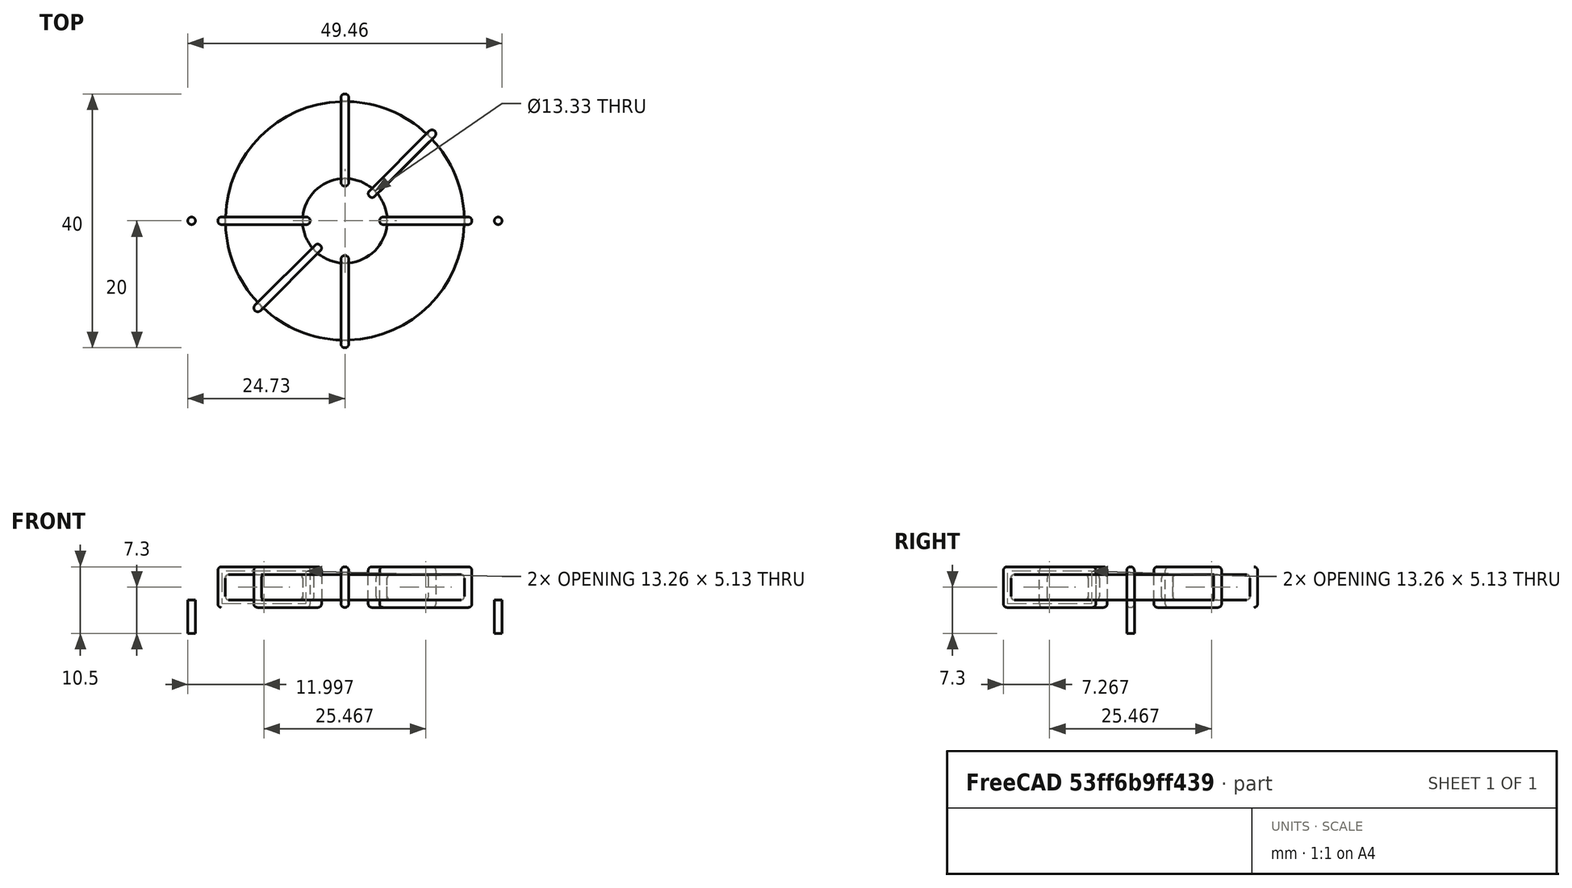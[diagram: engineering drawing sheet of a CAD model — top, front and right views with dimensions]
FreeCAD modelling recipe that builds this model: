
FCSTD DOCUMENT  (FreeCAD 0.16R6703 (Git))
Label: L_Toroid_Horizontal_D40.0mm_P48.26mm
License: All rights reserved
LicenseURL: http://en.wikipedia.org/wiki/All_rights_reserved
objects: Sketcher::SketchObject×6, PartDesign::Pad×6, PartDesign::Fillet×5, Spreadsheet::Sheet×1
note: 23 computed .brp shape members not serialized (recipe doc carries the construction recipe); baked Part::Feature solids carry a one-line shape summary decoded from their .brp

FEATURE [Spreadsheet::Sheet] Spreadsheet  label="dimensions"
  cells = A1=Wx; B1(Wx)=40; C1(WW)=13.33333333333333; D1=40; A2=Wy; B2(Wy)=40; D2=40; A3=RM; B3(RMx)=48.26; C3(RMy)=0; A4=d_wire; B4(d_wire)=1.2; A5=H; B5(H)=4; A6=offsetx; B6(offsetx)=-4.129999999999999
FEATURE [Sketcher::SketchObject] Sketch
  Placement = pos=(0,0,1.7) rot=(0,0,1;0rad)
  expr: Placement.Base.z = 0.5 + Spreadsheet.d_wire
  expr: Constraints[0] = Spreadsheet.Wx / 2 - Spreadsheet.d_wire
  expr: Constraints[4] = Spreadsheet.WW / 2
  expr: Constraints[2] = Spreadsheet.RMy / 2
  expr: Constraints[1] = Spreadsheet.RMx / 2
  sketch-geometry (2):
    g0: Circle CenterX=24.13 CenterY=0 CenterZ=0 NormalX=0 NormalY=0 NormalZ=1 Radius=18.8
    g1: Circle CenterX=24.13 CenterY=0 CenterZ=0 NormalX=0 NormalY=0 NormalZ=1 Radius=6.66667
  constraints (5):
    c: Radius(g0) = 18.8
    c: DistanceX(g-1,g0) = 24.13
    c: DistanceY(g-1,g0) = 0
    c: Coincident(g1,g0)
    c: Radius(g1) = 6.66667
FEATURE [PartDesign::Pad] Pad
  Length = 4
  Length2 = 100
  Placement = pos=(0,0,1.7) rot=(0,0,1;0rad)
  Sketch = -> Sketch
  Type = 0
  expr: Length = Spreadsheet.H
FEATURE [Sketcher::SketchObject] Sketch001
  Placement = pos=(0,0,1.1) rot=(0,0,1;0rad)
  expr: Placement.Base.z = 0.5 + Spreadsheet.d_wire * 0.5
  expr: Constraints[4] = Spreadsheet.RMx
  expr: Constraints[2] = Spreadsheet.RMy
  expr: Constraints[1] = Spreadsheet.d_wire / 2
  sketch-geometry (2):
    g0: Circle CenterX=0 CenterY=0 CenterZ=0 NormalX=0 NormalY=0 NormalZ=1 Radius=0.6
    g1: Circle CenterX=48.26 CenterY=0 CenterZ=0 NormalX=0 NormalY=0 NormalZ=1 Radius=0.6
  constraints (5):
    c: Equal(g0,g1)
    c: Radius(g0) = 0.6
    c: DistanceY(g-1,g1) = 0
    c: Coincident(g0,g-1)
    c: DistanceX(g-1,g1) = 48.26
FEATURE [PartDesign::Pad] Pad001
  Length = 0.6
  Length2 = 4.7
  Placement = pos=(0,0,1.1) rot=(0,0,1;0rad)
  Reversed = true
  Sketch = -> Sketch001
  Type = 4
  expr: Length2 = 3.5 + Spreadsheet.d_wire
  expr: Length = Spreadsheet.d_wire / 2
FEATURE [PartDesign::Fillet] Fillet
  Base = -> Pad [Edge6,Edge3,Edge2]
  Placement = pos=(0,0,1.7) rot=(0,0,1;0rad)
  Radius = 0.5
FEATURE [Sketcher::SketchObject] Sketch003
  Placement = pos=(24.13,0,0) rot=(1,0,0;1.5708rad)
  expr: Placement.Base.x = Spreadsheet.RMx / 2
  expr: Constraints[49] = Spreadsheet.Wx - Spreadsheet.d_wire * 2
  expr: Constraints[44] = Spreadsheet.d_wire
  expr: Constraints[23] = Spreadsheet.H
  expr: Constraints[22] = Spreadsheet.Wx / 2 - Spreadsheet.d_wire
  expr: Placement.Base.y = Spreadsheet.RMy / 2
  expr: Constraints[21] = (Spreadsheet.Wx - Spreadsheet.WW) / 2 - Spreadsheet.d_wire
  expr: Constraints[19] = Spreadsheet.d_wire
  expr: Constraints[17] = Spreadsheet.d_wire
  expr: Constraints[18] = Spreadsheet.d_wire
  expr: Constraints[16] = Spreadsheet.d_wire
  sketch-geometry (16):
    g0: LineSegment StartX=-5.46667 StartY=0.5 StartZ=0 EndX=-20 EndY=0.5 EndZ=0
    g1: LineSegment StartX=-20 StartY=0.5 StartZ=0 EndX=-20 EndY=6.9 EndZ=0
    g2: LineSegment StartX=-20 StartY=6.9 StartZ=0 EndX=-5.46667 EndY=6.9 EndZ=0
    g3: LineSegment StartX=-5.46667 StartY=6.9 StartZ=0 EndX=-5.46667 EndY=0.5 EndZ=0
    g4: LineSegment StartX=-18.8 StartY=5.7 StartZ=0 EndX=-6.66667 EndY=5.7 EndZ=0
    g5: LineSegment StartX=-6.66667 StartY=5.7 StartZ=0 EndX=-6.66667 EndY=1.7 EndZ=0
    g6: LineSegment StartX=-6.66667 StartY=1.7 StartZ=0 EndX=-18.8 EndY=1.7 EndZ=0
    g7: LineSegment StartX=-18.8 StartY=1.7 StartZ=0 EndX=-18.8 EndY=5.7 EndZ=0
    g8: LineSegment StartX=5.46667 StartY=6.9 StartZ=0 EndX=20 EndY=6.9 EndZ=0
    g9: LineSegment StartX=20 StartY=6.9 StartZ=0 EndX=20 EndY=0.5 EndZ=0
    g10: LineSegment StartX=20 StartY=0.5 StartZ=0 EndX=5.46667 EndY=0.5 EndZ=0
    g11: LineSegment StartX=5.46667 StartY=0.5 StartZ=0 EndX=5.46667 EndY=6.9 EndZ=0
    g12: LineSegment StartX=6.66667 StartY=5.7 StartZ=0 EndX=18.8 EndY=5.7 EndZ=0
    g13: LineSegment StartX=18.8 StartY=5.7 StartZ=0 EndX=18.8 EndY=1.7 EndZ=0
    g14: LineSegment StartX=18.8 StartY=1.7 StartZ=0 EndX=6.66667 EndY=1.7 EndZ=0
    g15: LineSegment StartX=6.66667 StartY=1.7 StartZ=0 EndX=6.66667 EndY=5.7 EndZ=0
  constraints (50):
    c: Horizontal(g0)
    c: Coincident(g1,g0)
    c: Vertical(g1)
    c: Coincident(g2,g1)
    c: Horizontal(g2)
    c: Coincident(g3,g2)
    c: Coincident(g3,g0)
    c: Vertical(g3)
    c: Coincident(g4,g5)
    c: Coincident(g5,g6)
    c: Coincident(g6,g7)
    c: Coincident(g7,g4)
    c: Horizontal(g4)
    c: Horizontal(g6)
    c: Vertical(g5)
    c: Vertical(g7)
    c: DistanceX(g1,g4) = 1.2
    c: DistanceY(g4,g1) = 1.2
    c: DistanceX(g5,g0) = 1.2
    c: DistanceY(g0,g5) = 1.2
    c: DistanceY(g-1,g0) = 0.5
    c: DistanceX(g6,g6) = 12.1333
    c: DistanceX(g6,g-1) = 18.8
    c: DistanceY(g7,g7) = 4
    c: Coincident(g8,g9)
    c: Coincident(g9,g10)
    c: Coincident(g10,g11)
    c: Coincident(g11,g8)
    c: Horizontal(g8)
    c: Horizontal(g10)
    c: Vertical(g9)
    c: Vertical(g11)
    c: Coincident(g12,g13)
    c: Coincident(g13,g14)
    c: Coincident(g14,g15)
    c: Coincident(g15,g12)
    c: Horizontal(g12)
    c: Horizontal(g14)
    c: Vertical(g13)
    c: Vertical(g15)
    c: DistanceY(g8,g2) = 0
    c: DistanceY(g10,g0) = 0
    c: DistanceY(g14,g5) = 0
    c: DistanceY(g12,g4) = 0
    c: DistanceX(g8,g12) = 1.2
    c: Equal(g8,g2)
    c: Equal(g12,g4)
    c: Equal(g9,g1)
    c: Equal(g13,g7)
    c: DistanceX(g4,g12) = 37.6
FEATURE [PartDesign::Pad] Pad002
  Length = 1.2
  Length2 = 100
  Midplane = true
  Placement = pos=(24.13,0,0) rot=(1,0,0;1.5708rad)
  Sketch = -> Sketch003
  Type = 0
  expr: Length = Spreadsheet.d_wire
FEATURE [PartDesign::Fillet] Fillet001
  Base = -> Pad002 [Edge38,Edge41,Edge42,Edge43,Edge29,Edge32,Edge33,Edge34,Edge25,Edge35,Edge36,Edge13,Edge14,Edge15,Edge16,Edge17,Edge18,Edge19,Edge1,Edge2,Edge3,Edge4,Edge5,Edge6,Edge7,Edge37,Edge39,Edge40,Edge20,Edge23,Edge24,Edge21,Edge22,Edge8,Edge9,Edge10,Edge11,Edge12,Edge26,Edge27,+8 more]
  Placement = pos=(24.13,0,0) rot=(1,0,0;1.5708rad)
  Radius = 0.564
  expr: Radius = Spreadsheet.d_wire * 0.47
FEATURE [Sketcher::SketchObject] Sketch004
  Placement = pos=(24.13,0,0) rot=(0.862856,0.357407,0.357407;1.71777rad)
  expr: Placement.Base.x = Spreadsheet.RMx / 2
  expr: Constraints[49] = Spreadsheet.Wx - 2 * Spreadsheet.d_wire
  expr: Constraints[44] = Spreadsheet.d_wire
  expr: Constraints[23] = Spreadsheet.H
  expr: Constraints[22] = Spreadsheet.Wx / 2 - Spreadsheet.d_wire
  expr: Placement.Base.y = Spreadsheet.RMy / 2
  expr: Constraints[21] = (Spreadsheet.Wx - Spreadsheet.WW) / 2 - Spreadsheet.d_wire
  expr: Constraints[19] = Spreadsheet.d_wire
  expr: Constraints[17] = Spreadsheet.d_wire
  expr: Constraints[18] = Spreadsheet.d_wire
  expr: Constraints[16] = Spreadsheet.d_wire
  sketch-geometry (16):
    g0: LineSegment StartX=-5.46667 StartY=0.5 StartZ=0 EndX=-20 EndY=0.5 EndZ=0
    g1: LineSegment StartX=-20 StartY=0.5 StartZ=0 EndX=-20 EndY=6.9 EndZ=0
    g2: LineSegment StartX=-20 StartY=6.9 StartZ=0 EndX=-5.46667 EndY=6.9 EndZ=0
    g3: LineSegment StartX=-5.46667 StartY=6.9 StartZ=0 EndX=-5.46667 EndY=0.5 EndZ=0
    g4: LineSegment StartX=-18.8 StartY=5.7 StartZ=0 EndX=-6.66667 EndY=5.7 EndZ=0
    g5: LineSegment StartX=-6.66667 StartY=5.7 StartZ=0 EndX=-6.66667 EndY=1.7 EndZ=0
    g6: LineSegment StartX=-6.66667 StartY=1.7 StartZ=0 EndX=-18.8 EndY=1.7 EndZ=0
    g7: LineSegment StartX=-18.8 StartY=1.7 StartZ=0 EndX=-18.8 EndY=5.7 EndZ=0
    g8: LineSegment StartX=5.46667 StartY=6.9 StartZ=0 EndX=20 EndY=6.9 EndZ=0
    g9: LineSegment StartX=20 StartY=6.9 StartZ=0 EndX=20 EndY=0.5 EndZ=0
    g10: LineSegment StartX=20 StartY=0.5 StartZ=0 EndX=5.46667 EndY=0.5 EndZ=0
    g11: LineSegment StartX=5.46667 StartY=0.5 StartZ=0 EndX=5.46667 EndY=6.9 EndZ=0
    g12: LineSegment StartX=6.66667 StartY=5.7 StartZ=0 EndX=18.8 EndY=5.7 EndZ=0
    g13: LineSegment StartX=18.8 StartY=5.7 StartZ=0 EndX=18.8 EndY=1.7 EndZ=0
    g14: LineSegment StartX=18.8 StartY=1.7 StartZ=0 EndX=6.66667 EndY=1.7 EndZ=0
    g15: LineSegment StartX=6.66667 StartY=1.7 StartZ=0 EndX=6.66667 EndY=5.7 EndZ=0
  constraints (50):
    c: Horizontal(g0)
    c: Coincident(g1,g0)
    c: Vertical(g1)
    c: Coincident(g2,g1)
    c: Horizontal(g2)
    c: Coincident(g3,g2)
    c: Coincident(g3,g0)
    c: Vertical(g3)
    c: Coincident(g4,g5)
    c: Coincident(g5,g6)
    c: Coincident(g6,g7)
    c: Coincident(g7,g4)
    c: Horizontal(g4)
    c: Horizontal(g6)
    c: Vertical(g5)
    c: Vertical(g7)
    c: DistanceX(g1,g4) = 1.2
    c: DistanceY(g4,g1) = 1.2
    c: DistanceX(g5,g0) = 1.2
    c: DistanceY(g0,g5) = 1.2
    c: DistanceY(g-1,g0) = 0.5
    c: DistanceX(g6,g6) = 12.1333
    c: DistanceX(g6,g-1) = 18.8
    c: DistanceY(g7,g7) = 4
    c: Coincident(g8,g9)
    c: Coincident(g9,g10)
    c: Coincident(g10,g11)
    c: Coincident(g11,g8)
    c: Horizontal(g8)
    c: Horizontal(g10)
    c: Vertical(g9)
    c: Vertical(g11)
    c: Coincident(g12,g13)
    c: Coincident(g13,g14)
    c: Coincident(g14,g15)
    c: Coincident(g15,g12)
    c: Horizontal(g12)
    c: Horizontal(g14)
    c: Vertical(g13)
    c: Vertical(g15)
    c: DistanceY(g8,g2) = 0
    c: DistanceY(g10,g0) = 0
    c: DistanceY(g14,g5) = 0
    c: DistanceY(g12,g4) = 0
    c: DistanceX(g8,g12) = 1.2
    c: Equal(g8,g2)
    c: Equal(g12,g4)
    c: Equal(g9,g1)
    c: Equal(g13,g7)
    c: DistanceX(g4,g12) = 37.6
FEATURE [PartDesign::Pad] Pad003
  Length = 1.2
  Length2 = 100
  Midplane = true
  Placement = pos=(24.13,0,0) rot=(0.862856,0.357407,0.357407;1.71777rad)
  Sketch = -> Sketch004
  Type = 0
  expr: Length = Spreadsheet.d_wire
FEATURE [PartDesign::Fillet] Fillet002
  Base = -> Pad003 [Edge38,Edge41,Edge42,Edge43,Edge29,Edge32,Edge33,Edge34,Edge25,Edge35,Edge36,Edge13,Edge14,Edge15,Edge16,Edge17,Edge18,Edge19,Edge1,Edge2,Edge3,Edge4,Edge5,Edge6,Edge7,Edge37,Edge39,Edge40,Edge20,Edge23,Edge24,Edge21,Edge22,Edge8,Edge9,Edge10,Edge11,Edge12,Edge26,Edge27,+8 more]
  Placement = pos=(24.13,0,0) rot=(0.862856,0.357407,0.357407;1.71777rad)
  Radius = 0.564
  expr: Radius = Spreadsheet.d_wire * 0.47
FEATURE [Sketcher::SketchObject] Sketch005
  Placement = pos=(24.13,0,0) rot=(0.862856,-0.357407,-0.357407;1.71777rad)
  expr: Placement.Base.x = Spreadsheet.RMx / 2
  expr: Constraints[49] = Spreadsheet.Wx - 2 * Spreadsheet.d_wire
  expr: Constraints[44] = Spreadsheet.d_wire
  expr: Constraints[23] = Spreadsheet.H
  expr: Constraints[22] = Spreadsheet.Wx / 2 - Spreadsheet.d_wire
  expr: Placement.Base.y = Spreadsheet.RMy / 2
  expr: Constraints[21] = (Spreadsheet.Wx - Spreadsheet.WW) / 2 - Spreadsheet.d_wire
  expr: Constraints[19] = Spreadsheet.d_wire
  expr: Constraints[17] = Spreadsheet.d_wire
  expr: Constraints[18] = Spreadsheet.d_wire
  expr: Constraints[16] = Spreadsheet.d_wire
  sketch-geometry (16):
    g0: LineSegment StartX=-5.46667 StartY=0.5 StartZ=0 EndX=-20 EndY=0.5 EndZ=0
    g1: LineSegment StartX=-20 StartY=0.5 StartZ=0 EndX=-20 EndY=6.9 EndZ=0
    g2: LineSegment StartX=-20 StartY=6.9 StartZ=0 EndX=-5.46667 EndY=6.9 EndZ=0
    g3: LineSegment StartX=-5.46667 StartY=6.9 StartZ=0 EndX=-5.46667 EndY=0.5 EndZ=0
    g4: LineSegment StartX=-18.8 StartY=5.7 StartZ=0 EndX=-6.66667 EndY=5.7 EndZ=0
    g5: LineSegment StartX=-6.66667 StartY=5.7 StartZ=0 EndX=-6.66667 EndY=1.7 EndZ=0
    g6: LineSegment StartX=-6.66667 StartY=1.7 StartZ=0 EndX=-18.8 EndY=1.7 EndZ=0
    g7: LineSegment StartX=-18.8 StartY=1.7 StartZ=0 EndX=-18.8 EndY=5.7 EndZ=0
    g8: LineSegment StartX=5.46667 StartY=6.9 StartZ=0 EndX=20 EndY=6.9 EndZ=0
    g9: LineSegment StartX=20 StartY=6.9 StartZ=0 EndX=20 EndY=0.5 EndZ=0
    g10: LineSegment StartX=20 StartY=0.5 StartZ=0 EndX=5.46667 EndY=0.5 EndZ=0
    g11: LineSegment StartX=5.46667 StartY=0.5 StartZ=0 EndX=5.46667 EndY=6.9 EndZ=0
    g12: LineSegment StartX=6.66667 StartY=5.7 StartZ=0 EndX=18.8 EndY=5.7 EndZ=0
    g13: LineSegment StartX=18.8 StartY=5.7 StartZ=0 EndX=18.8 EndY=1.7 EndZ=0
    g14: LineSegment StartX=18.8 StartY=1.7 StartZ=0 EndX=6.66667 EndY=1.7 EndZ=0
    g15: LineSegment StartX=6.66667 StartY=1.7 StartZ=0 EndX=6.66667 EndY=5.7 EndZ=0
  constraints (50):
    c: Horizontal(g0)
    c: Coincident(g1,g0)
    c: Vertical(g1)
    c: Coincident(g2,g1)
    c: Horizontal(g2)
    c: Coincident(g3,g2)
    c: Coincident(g3,g0)
    c: Vertical(g3)
    c: Coincident(g4,g5)
    c: Coincident(g5,g6)
    c: Coincident(g6,g7)
    c: Coincident(g7,g4)
    c: Horizontal(g4)
    c: Horizontal(g6)
    c: Vertical(g5)
    c: Vertical(g7)
    c: DistanceX(g1,g4) = 1.2
    c: DistanceY(g4,g1) = 1.2
    c: DistanceX(g5,g0) = 1.2
    c: DistanceY(g0,g5) = 1.2
    c: DistanceY(g-1,g0) = 0.5
    c: DistanceX(g6,g6) = 12.1333
    c: DistanceX(g6,g-1) = 18.8
    c: DistanceY(g7,g7) = 4
    c: Coincident(g8,g9)
    c: Coincident(g9,g10)
    c: Coincident(g10,g11)
    c: Coincident(g11,g8)
    c: Horizontal(g8)
    c: Horizontal(g10)
    c: Vertical(g9)
    c: Vertical(g11)
    c: Coincident(g12,g13)
    c: Coincident(g13,g14)
    c: Coincident(g14,g15)
    c: Coincident(g15,g12)
    c: Horizontal(g12)
    c: Horizontal(g14)
    c: Vertical(g13)
    c: Vertical(g15)
    c: DistanceY(g8,g2) = 0
    c: DistanceY(g10,g0) = 0
    c: DistanceY(g14,g5) = 0
    c: DistanceY(g12,g4) = 0
    c: DistanceX(g8,g12) = 1.2
    c: Equal(g8,g2)
    c: Equal(g12,g4)
    c: Equal(g9,g1)
    c: Equal(g13,g7)
    c: DistanceX(g4,g12) = 37.6
FEATURE [PartDesign::Pad] Pad004
  Length = 1.2
  Length2 = 100
  Midplane = true
  Placement = pos=(24.13,0,0) rot=(0.862856,-0.357407,-0.357407;1.71777rad)
  Sketch = -> Sketch005
  Type = 0
  expr: Length = Spreadsheet.d_wire
FEATURE [PartDesign::Fillet] Fillet003
  Base = -> Pad004 [Edge38,Edge41,Edge42,Edge43,Edge29,Edge32,Edge33,Edge34,Edge25,Edge35,Edge36,Edge13,Edge14,Edge15,Edge16,Edge17,Edge18,Edge19,Edge1,Edge2,Edge3,Edge4,Edge5,Edge6,Edge7,Edge37,Edge39,Edge40,Edge20,Edge23,Edge24,Edge21,Edge22,Edge8,Edge9,Edge10,Edge11,Edge12,Edge26,Edge27,+8 more]
  Placement = pos=(24.13,0,0) rot=(0.862856,-0.357407,-0.357407;1.71777rad)
  Radius = 0.564
  expr: Radius = Spreadsheet.d_wire * 0.47
FEATURE [Sketcher::SketchObject] Sketch006
  Placement = pos=(24.13,0,0) rot=(0.57735,0.57735,0.57735;2.0944rad)
  expr: Placement.Base.x = Spreadsheet.RMx / 2
  expr: Constraints[49] = Spreadsheet.Wx - Spreadsheet.d_wire * 2
  expr: Constraints[44] = Spreadsheet.d_wire
  expr: Constraints[23] = Spreadsheet.H
  expr: Constraints[22] = Spreadsheet.Wx / 2 - Spreadsheet.d_wire
  expr: Placement.Base.y = Spreadsheet.RMy / 2
  expr: Constraints[21] = (Spreadsheet.Wx - Spreadsheet.WW) / 2 - Spreadsheet.d_wire
  expr: Constraints[19] = Spreadsheet.d_wire
  expr: Constraints[17] = Spreadsheet.d_wire
  expr: Constraints[18] = Spreadsheet.d_wire
  expr: Constraints[16] = Spreadsheet.d_wire
  sketch-geometry (16):
    g0: LineSegment StartX=-5.46667 StartY=0.5 StartZ=0 EndX=-20 EndY=0.5 EndZ=0
    g1: LineSegment StartX=-20 StartY=0.5 StartZ=0 EndX=-20 EndY=6.9 EndZ=0
    g2: LineSegment StartX=-20 StartY=6.9 StartZ=0 EndX=-5.46667 EndY=6.9 EndZ=0
    g3: LineSegment StartX=-5.46667 StartY=6.9 StartZ=0 EndX=-5.46667 EndY=0.5 EndZ=0
    g4: LineSegment StartX=-18.8 StartY=5.7 StartZ=0 EndX=-6.66667 EndY=5.7 EndZ=0
    g5: LineSegment StartX=-6.66667 StartY=5.7 StartZ=0 EndX=-6.66667 EndY=1.7 EndZ=0
    g6: LineSegment StartX=-6.66667 StartY=1.7 StartZ=0 EndX=-18.8 EndY=1.7 EndZ=0
    g7: LineSegment StartX=-18.8 StartY=1.7 StartZ=0 EndX=-18.8 EndY=5.7 EndZ=0
    g8: LineSegment StartX=5.46667 StartY=6.9 StartZ=0 EndX=20 EndY=6.9 EndZ=0
    g9: LineSegment StartX=20 StartY=6.9 StartZ=0 EndX=20 EndY=0.5 EndZ=0
    g10: LineSegment StartX=20 StartY=0.5 StartZ=0 EndX=5.46667 EndY=0.5 EndZ=0
    g11: LineSegment StartX=5.46667 StartY=0.5 StartZ=0 EndX=5.46667 EndY=6.9 EndZ=0
    g12: LineSegment StartX=6.66667 StartY=5.7 StartZ=0 EndX=18.8 EndY=5.7 EndZ=0
    g13: LineSegment StartX=18.8 StartY=5.7 StartZ=0 EndX=18.8 EndY=1.7 EndZ=0
    g14: LineSegment StartX=18.8 StartY=1.7 StartZ=0 EndX=6.66667 EndY=1.7 EndZ=0
    g15: LineSegment StartX=6.66667 StartY=1.7 StartZ=0 EndX=6.66667 EndY=5.7 EndZ=0
  constraints (50):
    c: Horizontal(g0)
    c: Coincident(g1,g0)
    c: Vertical(g1)
    c: Coincident(g2,g1)
    c: Horizontal(g2)
    c: Coincident(g3,g2)
    c: Coincident(g3,g0)
    c: Vertical(g3)
    c: Coincident(g4,g5)
    c: Coincident(g5,g6)
    c: Coincident(g6,g7)
    c: Coincident(g7,g4)
    c: Horizontal(g4)
    c: Horizontal(g6)
    c: Vertical(g5)
    c: Vertical(g7)
    c: DistanceX(g1,g4) = 1.2
    c: DistanceY(g4,g1) = 1.2
    c: DistanceX(g5,g0) = 1.2
    c: DistanceY(g0,g5) = 1.2
    c: DistanceY(g-1,g0) = 0.5
    c: DistanceX(g6,g6) = 12.1333
    c: DistanceX(g6,g-1) = 18.8
    c: DistanceY(g7,g7) = 4
    c: Coincident(g8,g9)
    c: Coincident(g9,g10)
    c: Coincident(g10,g11)
    c: Coincident(g11,g8)
    c: Horizontal(g8)
    c: Horizontal(g10)
    c: Vertical(g9)
    c: Vertical(g11)
    c: Coincident(g12,g13)
    c: Coincident(g13,g14)
    c: Coincident(g14,g15)
    c: Coincident(g15,g12)
    c: Horizontal(g12)
    c: Horizontal(g14)
    c: Vertical(g13)
    c: Vertical(g15)
    c: DistanceY(g8,g2) = 0
    c: DistanceY(g10,g0) = 0
    c: DistanceY(g14,g5) = 0
    c: DistanceY(g12,g4) = 0
    c: DistanceX(g8,g12) = 1.2
    c: Equal(g8,g2)
    c: Equal(g12,g4)
    c: Equal(g9,g1)
    c: Equal(g13,g7)
    c: DistanceX(g4,g12) = 37.6
FEATURE [PartDesign::Pad] Pad005
  Length = 1.2
  Length2 = 100
  Midplane = true
  Placement = pos=(24.13,0,0) rot=(0.57735,0.57735,0.57735;2.0944rad)
  Sketch = -> Sketch006
  Type = 0
  expr: Length = Spreadsheet.d_wire
FEATURE [PartDesign::Fillet] Fillet004
  Base = -> Pad005 [Edge38,Edge41,Edge42,Edge43,Edge29,Edge32,Edge33,Edge34,Edge25,Edge35,Edge36,Edge13,Edge14,Edge15,Edge16,Edge17,Edge18,Edge19,Edge1,Edge2,Edge3,Edge4,Edge5,Edge6,Edge7,Edge37,Edge39,Edge40,Edge20,Edge23,Edge24,Edge21,Edge22,Edge8,Edge9,Edge10,Edge11,Edge12,Edge26,Edge27,+8 more]
  Placement = pos=(24.13,0,0) rot=(0.57735,0.57735,0.57735;2.0944rad)
  Radius = 0.564
  expr: Radius = Spreadsheet.d_wire * 0.47
